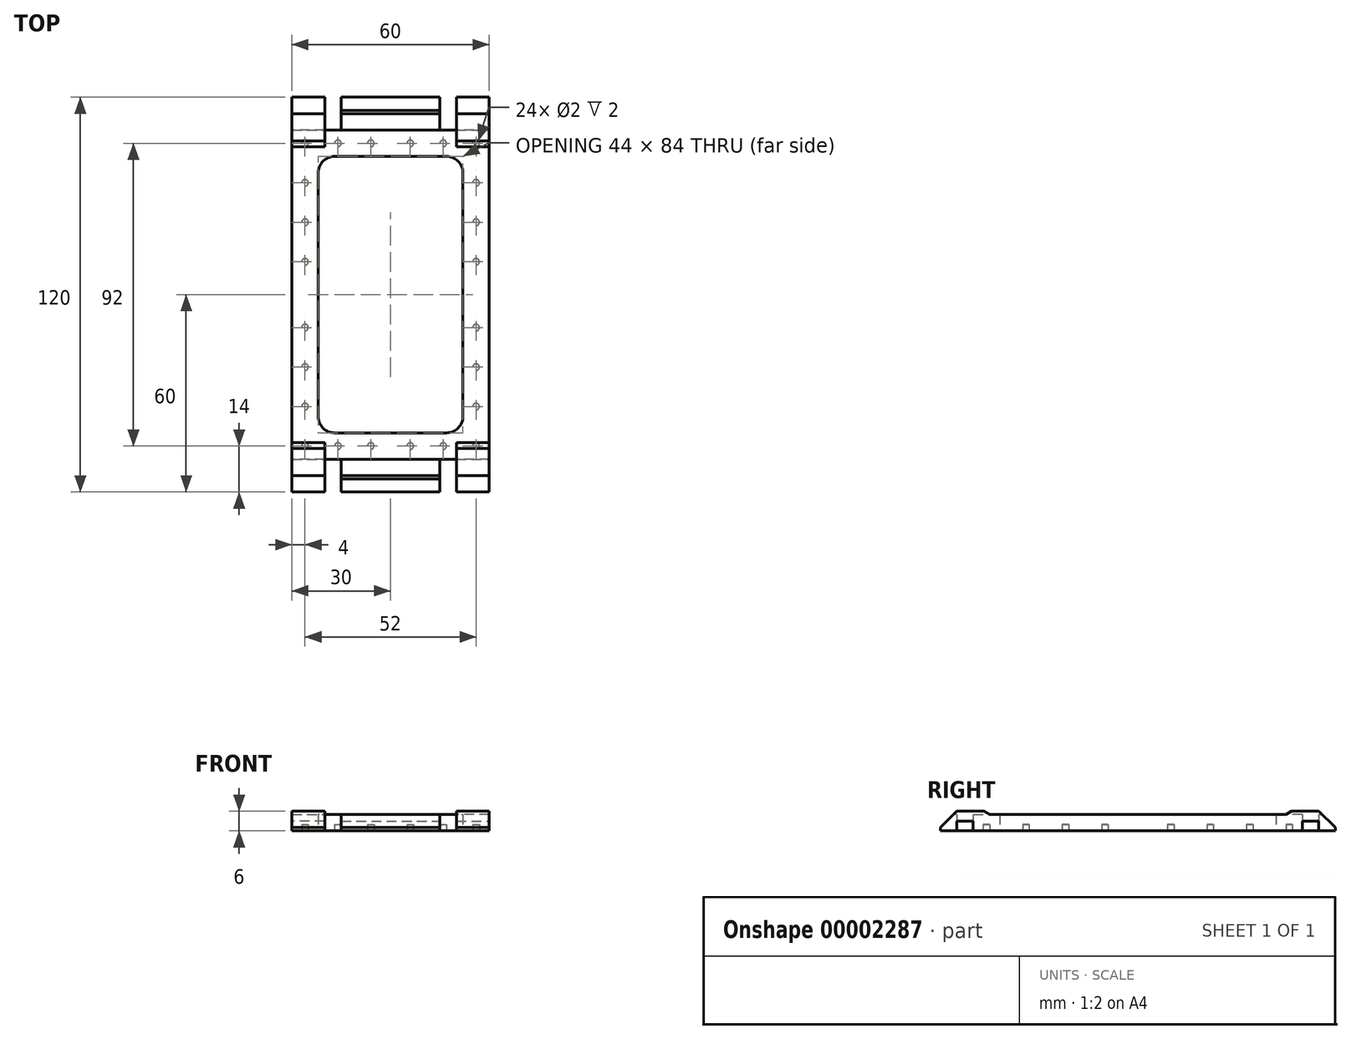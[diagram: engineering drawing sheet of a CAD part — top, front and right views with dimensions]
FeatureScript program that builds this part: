
annotation { "Feature Type Name" : "Feature", "Feature Type Description" : "" }
export const myFeature = defineFeature(function(context is Context, id is Id, definition is map)
    precondition{}
    {
        {
            var Q0;
            Q0=qCreatedBy(makeId("Top.planeOp"),FACE);
            var sketch = newSketch(context, id + "F0", { "sketchPlane" : qUnion([Q0])});
            skPoint(sketch, "E0.rect.middle", {"position": v(0, 0) * mm});
            skLineSegment(sketch, "E1", {"start": v(0, 50) * mm, "end": v(0, 0) * mm, "construction": true});
            skLineSegment(sketch, "E2.bottom", {"start": v(-30, 50) * mm, "end": v(-20, 50) * mm});
            skLineSegment(sketch, "E2.top", {"start": v(-30, 60) * mm, "end": v(-20, 60) * mm});
            skLineSegment(sketch, "E2.left", {"start": v(-30, 50) * mm, "end": v(-30, 60) * mm});
            skLineSegment(sketch, "E2.right", {"start": v(-20, 50) * mm, "end": v(-20, 60) * mm});
            skLineSegment(sketch, "E3.bottom", {"start": v(0, 50) * mm, "end": v(-15, 50) * mm});
            skLineSegment(sketch, "E3.top", {"start": v(0, 60) * mm, "end": v(-15, 60) * mm});
            skLineSegment(sketch, "E3.left", {"start": v(0, 50) * mm, "end": v(0, 60) * mm});
            skLineSegment(sketch, "E3.right", {"start": v(-15, 50) * mm, "end": v(-15, 60) * mm});
            skLineSegment(sketch, "E4", {"start": v(-30, 50) * mm, "end": v(-30, 0) * mm});
            skLineSegment(sketch, "E5", {"start": v(-20, 50) * mm, "end": v(-15, 50) * mm});
            skLineSegment(sketch, "E6", {"start": v(-30, 0) * mm, "end": v(-22, 0) * mm});
            skLineSegment(sketch, "E7", {"start": v(-22, 0) * mm, "end": v(-22, 37) * mm});
            skLineSegment(sketch, "E8", {"start": v(-17, 42) * mm, "end": v(0, 42) * mm});
            skLineSegment(sketch, "E9", {"start": v(0, 42) * mm, "end": v(0, 50) * mm});
            skLineSegment(sketch, "E10", {"start": v(-22, 0) * mm, "end": v(0, 0) * mm, "construction": true});
            skPoint(sketch, "E11.visualSharp", {"position": v(-22, 42) * mm});
            skArc(sketch, "E11.filletArc", {"start": v(-17, 42) * mm, "mid": v(-20.54, 40.54) * mm, "end": v(-22, 37) * mm});
            skSolve(sketch);
        }
        {
            var Q0;
            Q0 = qSketchRegion(id + "F0", true);
            extrude(context, id + "F1", {"entities" : qUnion([Q0]), "depth" : 5 * mm});
        }
        {
            var Q0;
            Q0=makeQuery(id+"F1.opExtrude","CAP_FACE",FACE,{"disambiguationData":[OSD([sQuery(id+"F0.wireOp",EDGE,"E0.rect.bottom"),sQuery(id+"F0.wireOp",EDGE,"E0.rect.left"),sQuery(id+"F0.wireOp",EDGE,"E0.rect.right"),sQuery(id+"F0.wireOp",EDGE,"E2.top"),sQuery(id+"F0.wireOp",EDGE,"E2.left"),sQuery(id+"F0.wireOp",EDGE,"E2.right"),sQuery(id+"F0.wireOp",EDGE,"E3.top"),sQuery(id+"F0.wireOp",EDGE,"E3.right"),sQuery(id+"F0.wireOp",EDGE,"8dd78533-71ad-427a-a356-95920263071d.0.MirrorCS"),sQuery(id+"F0.wireOp",EDGE,"a11a952b-e788-4085-9705-cff0ed95dc66.0.MirrorCS"),sQuery(id+"F0.wireOp",EDGE,"e45f0957-0954-452c-b698-723b5105295b.0.MirrorCS"),sQuery(id+"F0.wireOp",EDGE,"f61b77d5-9dc9-4dc6-a36b-fe702def4f4e.0.MirrorCS"),sQuery(id+"F0.wireOp",EDGE,"6235bd68-9394-4ea3-bb8d-64f7bd4e6ca2.0.MirrorCS"),sQuery(id+"F0.wireOp",EDGE,"5c020b64-50e3-4a5a-bb07-0855aa4a13f5.0.MirrorCS"),sQuery(id+"F0.wireOp",EDGE,"5c020b64-50e3-4a5a-bb07-0855aa4a13f5.1.MirrorCS"),sQuery(id+"F0.wireOp",EDGE,"5c020b64-50e3-4a5a-bb07-0855aa4a13f5.2.MirrorCS"),sQuery(id+"F0.wireOp",EDGE,"5c020b64-50e3-4a5a-bb07-0855aa4a13f5.3.MirrorCS"),sQuery(id+"F0.wireOp",EDGE,"5c020b64-50e3-4a5a-bb07-0855aa4a13f5.4.MirrorCS"),sQuery(id+"F0.wireOp",EDGE,"5c020b64-50e3-4a5a-bb07-0855aa4a13f5.6.MirrorCS"),sQuery(id+"F0.wireOp",EDGE,"5c020b64-50e3-4a5a-bb07-0855aa4a13f5.7.MirrorCS"),sQuery(id+"F0.wireOp",EDGE,"5c020b64-50e3-4a5a-bb07-0855aa4a13f5.9.MirrorCS"),sQuery(id+"F0.wireOp",EDGE,"5c020b64-50e3-4a5a-bb07-0855aa4a13f5.11.MirrorCS"),sQuery(id+"F0.wireOp",EDGE,"5c020b64-50e3-4a5a-bb07-0855aa4a13f5.12.MirrorCS"),sQuery(id+"F0.wireOp",EDGE,"5c020b64-50e3-4a5a-bb07-0855aa4a13f5.13.MirrorCS")])],"isStart":false});
            var sketch = newSketch(context, id + "F2", { "sketchPlane" : qUnion([Q0])});
            skLineSegment(sketch, "E12.bottom", {"start": v(-30, 60) * mm, "end": v(-20, 60) * mm});
            skLineSegment(sketch, "E12.top", {"start": v(-30, 45) * mm, "end": v(-20, 45) * mm});
            skLineSegment(sketch, "E12.left", {"start": v(-30, 60) * mm, "end": v(-30, 45) * mm});
            skLineSegment(sketch, "E12.right", {"start": v(-20, 60) * mm, "end": v(-20, 45) * mm});
            skSolve(sketch);
        }
        {
            var Q0;
            {var subQ3=sQuery(id+"F2.wireOp",EDGE,"E12.bottom");Q0=makeQuery(id+"F2.imprint","IMPRINT",FACE,{"disambiguationData":[TD([[makeQuery(id+"F2.imprint","IMPRINT",EDGE,{"derivedFrom":subQ3}),-1.0]])]});}
            extrude(context, id + "F3", {"entities" : qUnion([Q0]), "operationType" : NewBodyOperationType.ADD, "depth" : 1 * mm});
        }
        {
            var Q0;
            Q0=makeQuery(id+"F3.boolean.opBoolean","MERGE",FACE,{"derivedFrom":[makeQuery(id+"F1.opExtrude","SWEPT_FACE",FACE,{"disambiguationData":[OSD([sQuery(id+"F0.wireOp",EDGE,"E2.left"),sQuery(id+"F0.wireOp",EDGE,"E4")])]}),makeQuery(id+"F3.opExtrude","SWEPT_FACE",FACE,{"disambiguationData":[OSD([sQuery(id+"F2.wireOp",EDGE,"E12.left")])]})]});
            var sketch = newSketch(context, id + "F4", { "sketchPlane" : qUnion([Q0])});
            skLineSegment(sketch, "E13.bottom", {"start": v(-55, 0) * mm, "end": v(-50, 0) * mm});
            skLineSegment(sketch, "E13.top", {"start": v(-55, 3) * mm, "end": v(-50, 3) * mm});
            skLineSegment(sketch, "E13.left", {"start": v(-55, 0) * mm, "end": v(-55, 3) * mm});
            skLineSegment(sketch, "E13.right", {"start": v(-50, 0) * mm, "end": v(-50, 3) * mm});
            skLineSegment(sketch, "E14", {"start": v(-45, 6) * mm, "end": v(-45, 5) * mm});
            skLineSegment(sketch, "E15", {"start": v(-45, 5) * mm, "end": v(-46.73, 6) * mm});
            skLineSegment(sketch, "E16", {"start": v(-46.73, 6) * mm, "end": v(-45, 6) * mm});
            skSolve(sketch);
        }
        {
            var Q0;
            Q0 = qSketchRegion(id + "F4", true);
            extrude(context, id + "F5", {"entities" : qUnion([Q0]), "operationType" : NewBodyOperationType.REMOVE, "endBound" : BoundingType.UP_TO_NEXT, "oppositeDirection" : true, "depth" : 25 * mm});
        }
        {
            var Q0;
            Q0=makeQuery(id+"F1.opExtrude","SWEPT_FACE",FACE,{"disambiguationData":[OSD([sQuery(id+"F0.wireOp",EDGE,"E3.left"),sQuery(id+"F0.wireOp",EDGE,"360ef08f-bf87-405c-8a6f-2b79532a9f36")])]});
            var sketch = newSketch(context, id + "F6", { "sketchPlane" : qUnion([Q0])});
            skLineSegment(sketch, "E17.bottom", {"start": v(50, 5) * mm, "end": v(55, 5) * mm});
            skLineSegment(sketch, "E17.top", {"start": v(50, 3) * mm, "end": v(55, 3) * mm});
            skLineSegment(sketch, "E17.left", {"start": v(50, 5) * mm, "end": v(50, 3) * mm});
            skLineSegment(sketch, "E17.right", {"start": v(55, 5) * mm, "end": v(55, 3) * mm});
            skSolve(sketch);
        }
        {
            var Q0;
            Q0 = qSketchRegion(id + "F6", true);
            extrude(context, id + "F7", {"entities" : qUnion([Q0]), "operationType" : NewBodyOperationType.REMOVE, "endBound" : BoundingType.UP_TO_NEXT, "oppositeDirection" : true, "depth" : 25 * mm});
        }
        {
            var Q0;
            Q0=makeQuery(id+"F3.boolean.opBoolean","MERGE",FACE,{"derivedFrom":[makeQuery(id+"F1.opExtrude","SWEPT_FACE",FACE,{"disambiguationData":[OSD([sQuery(id+"F0.wireOp",EDGE,"E2.left"),sQuery(id+"F0.wireOp",EDGE,"E4")])]}),makeQuery(id+"F3.opExtrude","SWEPT_FACE",FACE,{"disambiguationData":[OSD([sQuery(id+"F2.wireOp",EDGE,"E12.left")])]})]});
            var sketch = newSketch(context, id + "F8", { "sketchPlane" : qUnion([Q0])});
            skLineSegment(sketch, "E18", {"start": v(-60, 6) * mm, "end": v(-55, 6) * mm});
            skLineSegment(sketch, "E19", {"start": v(-55, 6) * mm, "end": v(-60, 1) * mm});
            skLineSegment(sketch, "E20", {"start": v(-60, 1) * mm, "end": v(-60, 6) * mm});
            skSolve(sketch);
        }
        {
            var Q0;
            Q0 = qSketchRegion(id + "F8", true);
            extrude(context, id + "F9", {"entities" : qUnion([Q0]), "operationType" : NewBodyOperationType.REMOVE, "endBound" : BoundingType.THROUGH_ALL, "oppositeDirection" : true, "depth" : 25 * mm});
        }
        {
            var Q0;
            Q0=makeQuery(id+"F1.opExtrude","SWEPT_BODY",BODY,{"disambiguationData":[OSD([sQuery(id+"F0.wireOp",EDGE,"E2.top"),sQuery(id+"F0.wireOp",EDGE,"E2.left"),sQuery(id+"F0.wireOp",EDGE,"E2.right"),sQuery(id+"F0.wireOp",EDGE,"E3.top"),sQuery(id+"F0.wireOp",EDGE,"E3.right"),sQuery(id+"F0.wireOp",EDGE,"E3.left"),sQuery(id+"F0.wireOp",EDGE,"E4"),sQuery(id+"F0.wireOp",EDGE,"360ef08f-bf87-405c-8a6f-2b79532a9f36"),sQuery(id+"F0.wireOp",EDGE,"3a437d5b-f2c2-4767-a0a7-6e027f2b122c"),sQuery(id+"F0.wireOp",EDGE,"E5")])]});
            var Q1;
            Q1=qCreatedBy(makeId("Right.planeOp"),FACE);
            mirror(context, id + "F10", {"entities" : qUnion([Q0]), "mirrorPlane" : qUnion([Q1])});
        }
        {
            var Q0;
            Q0=makeQuery(id+"F10.opPattern","COPY",BODY,{"derivedFrom":makeQuery(id+"F1.opExtrude","SWEPT_BODY",BODY,{"disambiguationData":[OSD([sQuery(id+"F0.wireOp",EDGE,"E2.top"),sQuery(id+"F0.wireOp",EDGE,"E2.left"),sQuery(id+"F0.wireOp",EDGE,"E2.right"),sQuery(id+"F0.wireOp",EDGE,"E3.top"),sQuery(id+"F0.wireOp",EDGE,"E3.right"),sQuery(id+"F0.wireOp",EDGE,"E3.left"),sQuery(id+"F0.wireOp",EDGE,"E4"),sQuery(id+"F0.wireOp",EDGE,"360ef08f-bf87-405c-8a6f-2b79532a9f36"),sQuery(id+"F0.wireOp",EDGE,"3a437d5b-f2c2-4767-a0a7-6e027f2b122c"),sQuery(id+"F0.wireOp",EDGE,"E5")])]}),"instanceName":"1"});
            var Q1;
            Q1=makeQuery(id+"F1.opExtrude","SWEPT_BODY",BODY,{"disambiguationData":[OSD([sQuery(id+"F0.wireOp",EDGE,"E2.top"),sQuery(id+"F0.wireOp",EDGE,"E2.left"),sQuery(id+"F0.wireOp",EDGE,"E2.right"),sQuery(id+"F0.wireOp",EDGE,"E3.top"),sQuery(id+"F0.wireOp",EDGE,"E3.right"),sQuery(id+"F0.wireOp",EDGE,"E3.left"),sQuery(id+"F0.wireOp",EDGE,"E4"),sQuery(id+"F0.wireOp",EDGE,"360ef08f-bf87-405c-8a6f-2b79532a9f36"),sQuery(id+"F0.wireOp",EDGE,"3a437d5b-f2c2-4767-a0a7-6e027f2b122c"),sQuery(id+"F0.wireOp",EDGE,"E5")])]});
            var Q2;
            Q2=qCreatedBy(makeId("Front.planeOp"),FACE);
            mirror(context, id + "F11", {"entities" : qUnion([Q0, Q1]), "mirrorPlane" : qUnion([Q2])});
        }
        {
            var Q0;
            Q0=makeQuery(id+"F1.opExtrude","SWEPT_BODY",BODY,{"disambiguationData":[OSD([sQuery(id+"F0.wireOp",EDGE,"E2.top"),sQuery(id+"F0.wireOp",EDGE,"E2.left"),sQuery(id+"F0.wireOp",EDGE,"E2.right"),sQuery(id+"F0.wireOp",EDGE,"E3.top"),sQuery(id+"F0.wireOp",EDGE,"E3.right"),sQuery(id+"F0.wireOp",EDGE,"E3.left"),sQuery(id+"F0.wireOp",EDGE,"E4"),sQuery(id+"F0.wireOp",EDGE,"360ef08f-bf87-405c-8a6f-2b79532a9f36"),sQuery(id+"F0.wireOp",EDGE,"3a437d5b-f2c2-4767-a0a7-6e027f2b122c"),sQuery(id+"F0.wireOp",EDGE,"E5")])]});
            var Q1;
            Q1=makeQuery(id+"F10.opPattern","COPY",BODY,{"derivedFrom":makeQuery(id+"F1.opExtrude","SWEPT_BODY",BODY,{"disambiguationData":[OSD([sQuery(id+"F0.wireOp",EDGE,"E2.top"),sQuery(id+"F0.wireOp",EDGE,"E2.left"),sQuery(id+"F0.wireOp",EDGE,"E2.right"),sQuery(id+"F0.wireOp",EDGE,"E3.top"),sQuery(id+"F0.wireOp",EDGE,"E3.right"),sQuery(id+"F0.wireOp",EDGE,"E3.left"),sQuery(id+"F0.wireOp",EDGE,"E4"),sQuery(id+"F0.wireOp",EDGE,"360ef08f-bf87-405c-8a6f-2b79532a9f36"),sQuery(id+"F0.wireOp",EDGE,"3a437d5b-f2c2-4767-a0a7-6e027f2b122c"),sQuery(id+"F0.wireOp",EDGE,"E5")])]}),"instanceName":"1"});
            var Q2;
            Q2=makeQuery(id+"F11.opPattern","COPY",BODY,{"derivedFrom":makeQuery(id+"F1.opExtrude","SWEPT_BODY",BODY,{"disambiguationData":[OSD([sQuery(id+"F0.wireOp",EDGE,"E2.top"),sQuery(id+"F0.wireOp",EDGE,"E2.left"),sQuery(id+"F0.wireOp",EDGE,"E2.right"),sQuery(id+"F0.wireOp",EDGE,"E3.top"),sQuery(id+"F0.wireOp",EDGE,"E3.right"),sQuery(id+"F0.wireOp",EDGE,"E3.left"),sQuery(id+"F0.wireOp",EDGE,"E4"),sQuery(id+"F0.wireOp",EDGE,"360ef08f-bf87-405c-8a6f-2b79532a9f36"),sQuery(id+"F0.wireOp",EDGE,"3a437d5b-f2c2-4767-a0a7-6e027f2b122c"),sQuery(id+"F0.wireOp",EDGE,"E5")])]}),"instanceName":"1"});
            var Q3;
            Q3=makeQuery(id+"F11.opPattern","COPY",BODY,{"derivedFrom":makeQuery(id+"F10.opPattern","COPY",BODY,{"derivedFrom":makeQuery(id+"F1.opExtrude","SWEPT_BODY",BODY,{"disambiguationData":[OSD([sQuery(id+"F0.wireOp",EDGE,"E2.top"),sQuery(id+"F0.wireOp",EDGE,"E2.left"),sQuery(id+"F0.wireOp",EDGE,"E2.right"),sQuery(id+"F0.wireOp",EDGE,"E3.top"),sQuery(id+"F0.wireOp",EDGE,"E3.right"),sQuery(id+"F0.wireOp",EDGE,"E3.left"),sQuery(id+"F0.wireOp",EDGE,"E4"),sQuery(id+"F0.wireOp",EDGE,"360ef08f-bf87-405c-8a6f-2b79532a9f36"),sQuery(id+"F0.wireOp",EDGE,"3a437d5b-f2c2-4767-a0a7-6e027f2b122c"),sQuery(id+"F0.wireOp",EDGE,"E5")])]}),"instanceName":"1"}),"instanceName":"1"});
            booleanBodies(context, id + "F12", {"operationType" : BooleanOperationType.UNION, "tools" : qUnion([Q0, Q1, Q2, Q3])});
        }
        {
            var Q0;
            {var subQ0=sQuery(id+"F0.wireOp",EDGE,"E2.left");var subQ1=sQuery(id+"F0.wireOp",EDGE,"E3.top");var subQ2=sQuery(id+"F0.wireOp",EDGE,"E3.right");var subQ3=sQuery(id+"F0.wireOp",EDGE,"E3.left");var subQ4=sQuery(id+"F0.wireOp",EDGE,"E4");var subQ5=sQuery(id+"F0.wireOp",EDGE,"E5");var subQ6=sQuery(id+"F0.wireOp",EDGE,"E6");var subQ7=sQuery(id+"F0.wireOp",EDGE,"E7");var subQ8=sQuery(id+"F0.wireOp",EDGE,"E8");var subQ9=sQuery(id+"F0.wireOp",EDGE,"E9");var subQ10=sQuery(id+"F0.wireOp",EDGE,"E11.filletArc");var subQ11=makeQuery(id+"F5.boolean.opBoolean","SPLIT",FACE,{"disambiguationData":[TD([makeQuery(id+"F1.opExtrude","SWEPT_FACE",FACE,{"disambiguationData":[OSD([subQ1])]})])],"derivedFrom":makeQuery(id+"F1.opExtrude","CAP_FACE",FACE,{"disambiguationData":[OSD([sQuery(id+"F0.wireOp",EDGE,"E2.top"),subQ0,sQuery(id+"F0.wireOp",EDGE,"E2.right"),subQ1,subQ2,subQ3,subQ4,subQ5,subQ6,subQ7,subQ8,subQ9,subQ10])],"isStart":true})});var subQ12=makeQuery(id+"F10.opPattern","COPY",FACE,{"derivedFrom":subQ11,"instanceName":"1"});Q0=makeQuery(id+"F12.opBoolean","MERGE",FACE,{"derivedFrom":[subQ11,subQ12,makeQuery(id+"F11.opPattern","COPY",FACE,{"derivedFrom":subQ11,"instanceName":"1"}),makeQuery(id+"F11.opPattern","COPY",FACE,{"derivedFrom":subQ12,"instanceName":"1"})]});}
            var sketch = newSketch(context, id + "F13", { "sketchPlane" : qUnion([Q0])});
            skCircle(sketch, "E21", {"center": v(-26, 46) * mm, "radius": 1 * mm});
            skCircle(sketch, "E22.1.0.0", {"center": v(-16, 46) * mm, "radius": 1 * mm});
            skCircle(sketch, "E22.2.0.0", {"center": v(-6, 46) * mm, "radius": 1 * mm});
            skLineSegment(sketch, "E22.direction1", {"start": v(-26, 46) * mm, "end": v(-16, 46) * mm, "construction": true});
            skCircle(sketch, "E23.0.1.0", {"center": v(-26, 34) * mm, "radius": 1 * mm});
            skCircle(sketch, "E23.0.2.0", {"center": v(-26, 22) * mm, "radius": 1 * mm});
            skCircle(sketch, "E23.0.3.0", {"center": v(-26, 10) * mm, "radius": 1 * mm});
            skLineSegment(sketch, "E23.direction1", {"start": v(-26, 46) * mm, "end": v(-1, 46) * mm, "construction": true});
            skLineSegment(sketch, "E23.direction2", {"start": v(-26, 46) * mm, "end": v(-26, 34) * mm, "construction": true});
            skLineSegment(sketch, "E24", {"start": v(0, 60) * mm, "end": v(0, 0) * mm, "construction": true});
            skLineSegment(sketch, "E25", {"start": v(0, 0) * mm, "end": v(-30, 0) * mm, "construction": true});
            skCircle(sketch, "E26.0.MirrorC", {"center": v(6, 46) * mm, "radius": 1 * mm});
            skCircle(sketch, "E26.1.MirrorC", {"center": v(26, 10) * mm, "radius": 1 * mm});
            skLineSegment(sketch, "E26.2.MirrorCS", {"start": v(26, 46) * mm, "end": v(26, 34) * mm, "construction": true});
            skLineSegment(sketch, "E26.3.MirrorCS", {"start": v(26, 46) * mm, "end": v(16, 46) * mm, "construction": true});
            skLineSegment(sketch, "E26.4.MirrorCS", {"start": v(26, 46) * mm, "end": v(1, 46) * mm, "construction": true});
            skCircle(sketch, "E26.5.MirrorC", {"center": v(16, 46) * mm, "radius": 1 * mm});
            skCircle(sketch, "E26.6.MirrorC", {"center": v(26, 46) * mm, "radius": 1 * mm});
            skCircle(sketch, "E26.7.MirrorC", {"center": v(26, 34) * mm, "radius": 1 * mm});
            skCircle(sketch, "E26.8.MirrorC", {"center": v(26, 22) * mm, "radius": 1 * mm});
            skLineSegment(sketch, "E27.0.MirrorCS", {"start": v(26, -46) * mm, "end": v(16, -46) * mm, "construction": true});
            skLineSegment(sketch, "E27.1.MirrorCS", {"start": v(0, -60) * mm, "end": v(0, 0) * mm, "construction": true});
            skCircle(sketch, "E27.2.MirrorC", {"center": v(26, -34) * mm, "radius": 1 * mm});
            skCircle(sketch, "E27.3.MirrorC", {"center": v(-6, -46) * mm, "radius": 1 * mm});
            skLineSegment(sketch, "E27.4.MirrorCS", {"start": v(-26, -46) * mm, "end": v(-16, -46) * mm, "construction": true});
            skCircle(sketch, "E27.5.MirrorC", {"center": v(-26, -34) * mm, "radius": 1 * mm});
            skCircle(sketch, "E27.6.MirrorC", {"center": v(-26, -22) * mm, "radius": 1 * mm});
            skLineSegment(sketch, "E27.7.MirrorCS", {"start": v(26, -46) * mm, "end": v(1, -46) * mm, "construction": true});
            skCircle(sketch, "E27.8.MirrorC", {"center": v(-26, -46) * mm, "radius": 1 * mm});
            skCircle(sketch, "E27.9.MirrorC", {"center": v(-16, -46) * mm, "radius": 1 * mm});
            skLineSegment(sketch, "E27.10.MirrorCS", {"start": v(26, -46) * mm, "end": v(26, -34) * mm, "construction": true});
            skCircle(sketch, "E27.11.MirrorC", {"center": v(16, -46) * mm, "radius": 1 * mm});
            skLineSegment(sketch, "E27.12.MirrorCS", {"start": v(-26, -46) * mm, "end": v(-26, -34) * mm, "construction": true});
            skCircle(sketch, "E27.13.MirrorC", {"center": v(6, -46) * mm, "radius": 1 * mm});
            skCircle(sketch, "E27.14.MirrorC", {"center": v(-26, -10) * mm, "radius": 1 * mm});
            skLineSegment(sketch, "E27.15.MirrorCS", {"start": v(-26, -46) * mm, "end": v(-1, -46) * mm, "construction": true});
            skCircle(sketch, "E27.16.MirrorC", {"center": v(26, -10) * mm, "radius": 1 * mm});
            skCircle(sketch, "E27.17.MirrorC", {"center": v(26, -22) * mm, "radius": 1 * mm});
            skCircle(sketch, "E27.18.MirrorC", {"center": v(26, -46) * mm, "radius": 1 * mm});
            skSolve(sketch);
        }
        {
            var Q0;
            Q0 = qSketchRegion(id + "F13", true);
            extrude(context, id + "F14", {"entities" : qUnion([Q0]), "operationType" : NewBodyOperationType.REMOVE, "oppositeDirection" : true, "depth" : 2 * mm});
        }
    });
